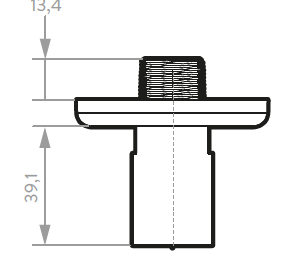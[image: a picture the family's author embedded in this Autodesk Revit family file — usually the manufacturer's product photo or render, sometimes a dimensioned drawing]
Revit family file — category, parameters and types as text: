
# Revit family: 704320001_Ducha Antivandálica con Regadera de Seguridad
name_source: partatom
category: Plumbing Fixtures
units: mm (PartAtom-declared; Revit-internal decimal feet)

## family parameters
Always vertical = Yes
Cut with Voids When Loaded = No
Host = Wall
OmniClass Number = 23.31.11.00
OmniClass Title = Faucets
Part Type = Normal
Room Calculation Point = No
Round Connector Dimension = Use Diameter
Shared = No

## types (1)
- Type 1
    Alto = 850 mm  [stored 2.78871 ft]
    Capacidad de flujo máximo por norma = 6,6L/min - 3,3L /Descarga a 80 Psi
    Creado por = BIMBAU
    Default Elevation = 0 mm  [stored 0 ft]
    Description = Nuestra grifería de lavamanos antivandálica viene con pico de seguridad y accionamiento tipo push. Con cierre automático temporizado
    Fecha de creación = 16/03/2021
    Garantía = 1 Año
    Manufacturer = Corona
    Material = Corona_Aluminio
    Material 2 = Corona_Cobre
    Model = Push Pico de Seguridad
    Peso Bruto aprox = 799gr. / 1,76Lb
    Peso Neto aprox = 726gr. / 1,60Lb
    Presion maxima = 80 Psi
    Presion minima = 20 Psi
    Referencia = 701320001
    URL = https://corona.co
    Vida útil = 150,000 ciclos.

note: [stored X ft] marks values corroborated as IEEE doubles in the binary element streams (Revit-internal decimal feet)

## geometry (parser evidence)
native form markers: Sweep x8
no freeform markers — native parametric forms only
